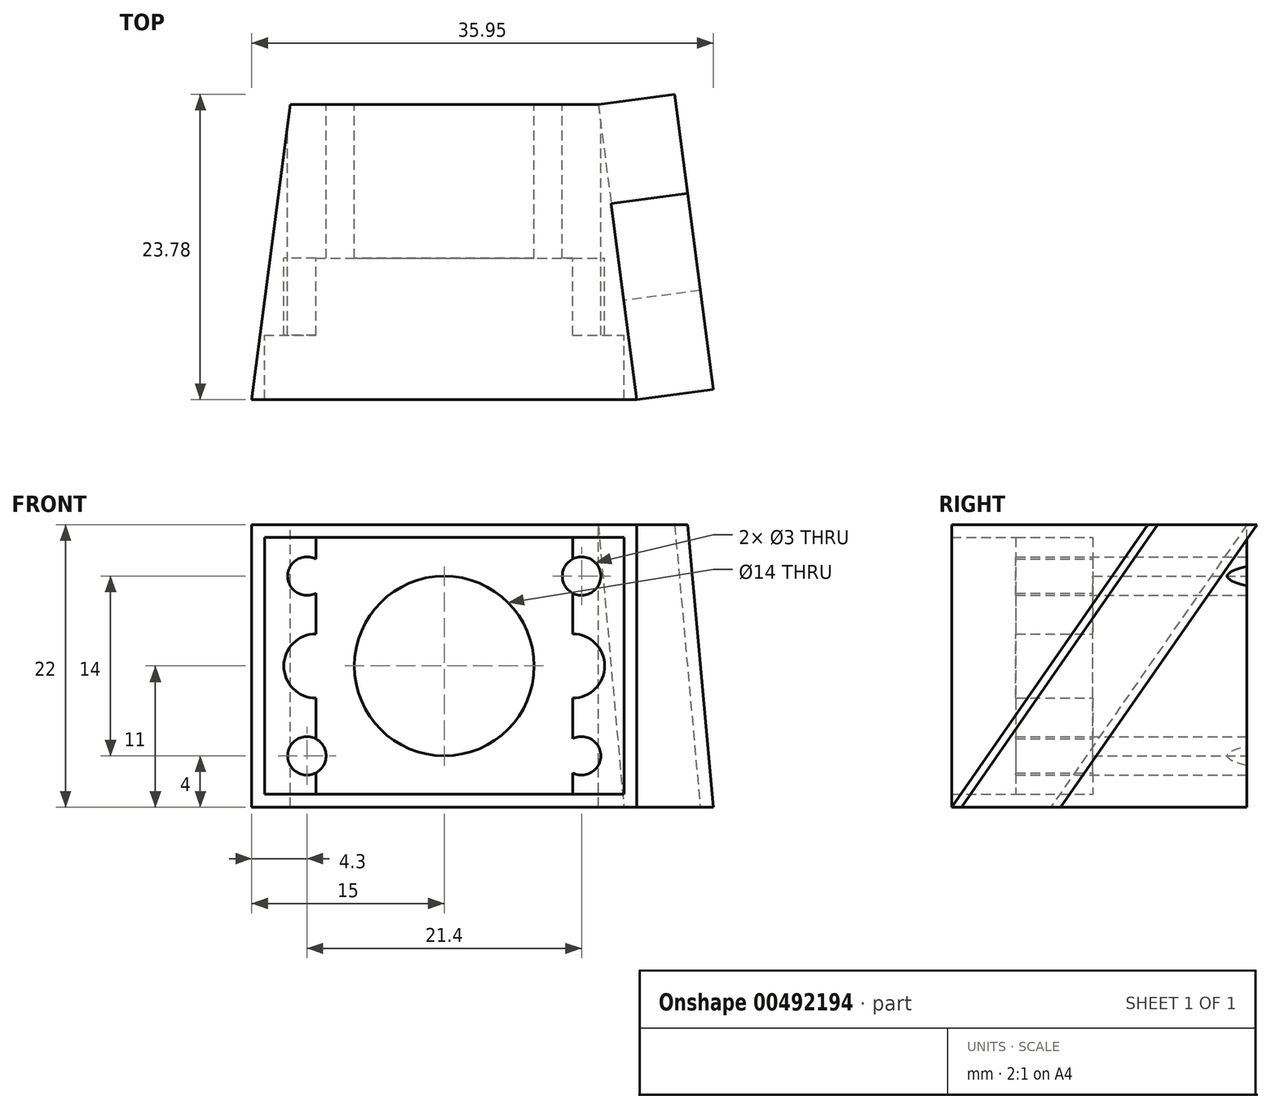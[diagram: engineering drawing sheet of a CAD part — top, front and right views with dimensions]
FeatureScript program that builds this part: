
annotation { "Feature Type Name" : "Feature", "Feature Type Description" : "" }
export const myFeature = defineFeature(function(context is Context, id is Id, definition is map)
    precondition{}
    {
        {
            var Q0;
            Q0=qCreatedBy(makeId("Front.planeOp"),FACE);
            var sketch = newSketch(context, id + "F0", { "sketchPlane" : qUnion([Q0])});
            skLineSegment(sketch, "E0.bottom", {"start": v(-15, 0) * mm, "end": v(15, 0) * mm});
            skLineSegment(sketch, "E0.top", {"start": v(-15, -22) * mm, "end": v(15, -22) * mm});
            skLineSegment(sketch, "E0.left", {"start": v(-15, 0) * mm, "end": v(-15, -22) * mm});
            skLineSegment(sketch, "E0.right", {"start": v(15, 0) * mm, "end": v(15, -22) * mm});
            skLineSegment(sketch, "E1.bottom", {"start": v(-14, -1) * mm, "end": v(14, -1) * mm});
            skLineSegment(sketch, "E1.top", {"start": v(-14, -21) * mm, "end": v(14, -21) * mm});
            skLineSegment(sketch, "E1.left", {"start": v(-14, -1) * mm, "end": v(-14, -21) * mm});
            skLineSegment(sketch, "E1.right", {"start": v(14, -1) * mm, "end": v(14, -21) * mm});
            skCircle(sketch, "E2", {"center": v(-10.7, -4) * mm, "radius": 1.5 * mm});
            skCircle(sketch, "E3.MirrorC", {"center": v(10.7, -4) * mm, "radius": 1.5 * mm});
            skLineSegment(sketch, "E4", {"start": v(-15, -11) * mm, "end": v(15, -11) * mm, "construction": true});
            skCircle(sketch, "E5.MirrorC", {"center": v(-10.7, -18) * mm, "radius": 1.5 * mm});
            skCircle(sketch, "E6.MirrorC", {"center": v(10.7, -18) * mm, "radius": 1.5 * mm});
            skLineSegment(sketch, "E7", {"start": v(0, 10.62) * mm, "end": v(0, -33.66) * mm, "construction": true});
            skCircle(sketch, "E8", {"center": v(0, -11) * mm, "radius": 7 * mm});
            skLineSegment(sketch, "E9", {"start": v(-10, -1) * mm, "end": v(-10, -2.67) * mm});
            skLineSegment(sketch, "E10.MirrorCS", {"start": v(10, -1) * mm, "end": v(10, -2.67) * mm});
            skArc(sketch, "E11", {"start": v(-10, -8.5) * mm, "mid": v(-12.5, -11) * mm, "end": v(-10, -13.5) * mm});
            skLineSegment(sketch, "E12.trimOffspring", {"start": v(-10, -13.5) * mm, "end": v(-10, -16.67) * mm});
            skArc(sketch, "E13.MirrorCS", {"start": v(10, -8.5) * mm, "mid": v(12.5, -11) * mm, "end": v(10, -13.5) * mm});
            skLineSegment(sketch, "E14.trimOffspring", {"start": v(10, -13.5) * mm, "end": v(10, -16.67) * mm});
            skLineSegment(sketch, "E15.trimOffspring", {"start": v(-10, -5.33) * mm, "end": v(-10, -8.5) * mm});
            skLineSegment(sketch, "E16.trimOffspring", {"start": v(10, -5.33) * mm, "end": v(10, -8.5) * mm});
            skLineSegment(sketch, "E17.trimOffspring", {"start": v(10, -19.33) * mm, "end": v(10, -21) * mm});
            skLineSegment(sketch, "E18.trimOffspring", {"start": v(-10, -19.33) * mm, "end": v(-10, -21) * mm});
            skSolve(sketch);
        }
        {
            var Q0;
            Q0 = qSketchRegion(id + "F0", true);
            extrude(context, id + "F1", {"entities" : qUnion([Q0]), "depth" : 23 * mm});
        }
        {
            var Q0;
            {var subQ0=sQuery(id+"F0.wireOp",EDGE,"E1.left");Q0=makeQuery(id+"F0.imprint","IMPRINT",FACE,{"disambiguationData":[TD([[makeQuery(id+"F0.imprint","IMPRINT",EDGE,{"derivedFrom":subQ0}),1.0]])]});}
            var Q1;
            {var subQ3=sQuery(id+"F0.wireOp",EDGE,"E1.right");Q1=makeQuery(id+"F0.imprint","IMPRINT",FACE,{"disambiguationData":[TD([[makeQuery(id+"F0.imprint","IMPRINT",EDGE,{"derivedFrom":subQ3}),-1.0]])]});}
            extrude(context, id + "F2", {"entities" : qUnion([Q0, Q1]), "operationType" : NewBodyOperationType.ADD, "depth" : 18 * mm});
        }
        {
            var Q0;
            Q0=makeQuery(id+"F0.imprint","IMPRINT",FACE,{"disambiguationData":[TD([[makeQuery(id+"F0.imprint","IMPRINT",EDGE,{"derivedFrom":sQuery(id+"F0.wireOp",EDGE,"E8")}),-1.0]])]});
            extrude(context, id + "F3", {"entities" : qUnion([Q0]), "operationType" : NewBodyOperationType.ADD, "depth" : 12 * mm});
        }
        {
            var Q0;
            {var subQ0=sQuery(id+"F0.wireOp",EDGE,"E2");var subQ1=makeQuery(id+"F0.imprint","INTERSECT",VERTEX,{"derivedFrom":[subQ0,sQuery(id+"F0.wireOp",EDGE,"E9")]});Q0=makeQuery(id+"F0.imprint","IMPRINT",FACE,{"disambiguationData":[TD([[makeQuery(id+"F0.imprint","IMPRINT",EDGE,{"disambiguationData":[TD([[subQ1,-1.0]])],"derivedFrom":subQ0}),1.0]])]});}
            var Q1;
            {var subQ0=sQuery(id+"F0.wireOp",EDGE,"E3.MirrorC");var subQ1=makeQuery(id+"F0.imprint","INTERSECT",VERTEX,{"derivedFrom":[subQ0,sQuery(id+"F0.wireOp",EDGE,"E10.MirrorCS")]});Q1=makeQuery(id+"F0.imprint","IMPRINT",FACE,{"disambiguationData":[TD([[makeQuery(id+"F0.imprint","IMPRINT",EDGE,{"disambiguationData":[TD([[subQ1,-1.0]])],"derivedFrom":subQ0}),-1.0]])]});}
            var Q2;
            {var subQ0=sQuery(id+"F0.wireOp",EDGE,"E6.MirrorC");var subQ1=makeQuery(id+"F0.imprint","INTERSECT",VERTEX,{"derivedFrom":[subQ0,sQuery(id+"F0.wireOp",EDGE,"E14.trimOffspring")]});Q2=makeQuery(id+"F0.imprint","IMPRINT",FACE,{"disambiguationData":[TD([[makeQuery(id+"F0.imprint","IMPRINT",EDGE,{"disambiguationData":[TD([[subQ1,1.0]])],"derivedFrom":subQ0}),1.0]])]});}
            var Q3;
            {var subQ0=sQuery(id+"F0.wireOp",EDGE,"E5.MirrorC");var subQ1=makeQuery(id+"F0.imprint","INTERSECT",VERTEX,{"derivedFrom":[subQ0,sQuery(id+"F0.wireOp",EDGE,"E12.trimOffspring")]});Q3=makeQuery(id+"F0.imprint","IMPRINT",FACE,{"disambiguationData":[TD([[makeQuery(id+"F0.imprint","IMPRINT",EDGE,{"disambiguationData":[TD([[subQ1,1.0]])],"derivedFrom":subQ0}),-1.0]])]});}
            extrude(context, id + "F4", {"entities" : qUnion([Q0, Q1, Q2, Q3]), "operationType" : NewBodyOperationType.ADD, "depth" : 12 * mm});
        }
        {
            var Q0;
            Q0=makeQuery(id+"F1.opExtrude","SWEPT_FACE",FACE,{"disambiguationData":[OSD([sQuery(id+"F0.wireOp",EDGE,"E0.bottom")])]});
            var sketch = newSketch(context, id + "F5", { "sketchPlane" : qUnion([Q0])});
            skLineSegment(sketch, "E19", {"start": v(-12, 0) * mm, "end": v(-15, -23) * mm});
            skLineSegment(sketch, "E20", {"start": v(0, 0) * mm, "end": v(0, -28.13) * mm, "construction": true});
            skLineSegment(sketch, "E21.MirrorCS", {"start": v(12, 0) * mm, "end": v(15, -23) * mm});
            skSolve(sketch);
        }
        {
            var Q0;
            {var subQ0=sQuery(id+"F5.wireOp",EDGE,"E19");Q0=makeQuery(id+"F5.imprint","IMPRINT",FACE,{"disambiguationData":[TD([[makeQuery(id+"F5.imprint","IMPRINT",EDGE,{"derivedFrom":subQ0}),-1.0]])]});}
            var Q1;
            {var subQ0=sQuery(id+"F5.wireOp",EDGE,"E21.MirrorCS");Q1=makeQuery(id+"F5.imprint","IMPRINT",FACE,{"disambiguationData":[TD([[makeQuery(id+"F5.imprint","IMPRINT",EDGE,{"derivedFrom":subQ0}),1.0]])]});}
            extrude(context, id + "F6", {"entities" : qUnion([Q0, Q1]), "operationType" : NewBodyOperationType.REMOVE, "oppositeDirection" : true, "depth" : 25 * mm});
        }
        {
            var Q0;
            Q0=makeQuery(id+"F6.boolean.opBoolean","COPY",FACE,{"derivedFrom":makeQuery(id+"F6.opExtrude","SWEPT_FACE",FACE,{"disambiguationData":[OSD([sQuery(id+"F5.wireOp",EDGE,"E21.MirrorCS")])]})});
            var sketch = newSketch(context, id + "F7", { "sketchPlane" : qUnion([Q0])});
            skLineSegment(sketch, "E22", {"start": v(-9.34, 0) * mm, "end": v(-24.75, -22) * mm});
            skLineSegment(sketch, "E23", {"start": v(-1.55, 0) * mm, "end": v(-16.96, -22) * mm});
            skSolve(sketch);
        }
        {
            var Q0;
            Q0 = qSketchRegion(id + "F7", true);
            var Q1;
            {var subQ0=sQuery(id+"F7.wireOp",EDGE,"E22");Q1=makeQuery(id+"F7.imprint","IMPRINT",FACE,{"disambiguationData":[TD([[makeQuery(id+"F7.imprint","IMPRINT",EDGE,{"derivedFrom":subQ0}),1.0]])]});}
            var Q2;
            Q2 = qSketchRegion(id + "F5", true);
            extrude(context, id + "F8", {"entities" : qUnion([Q0, Q1, Q2]), "operationType" : NewBodyOperationType.ADD, "depth" : 6 * mm});
        }
    });
